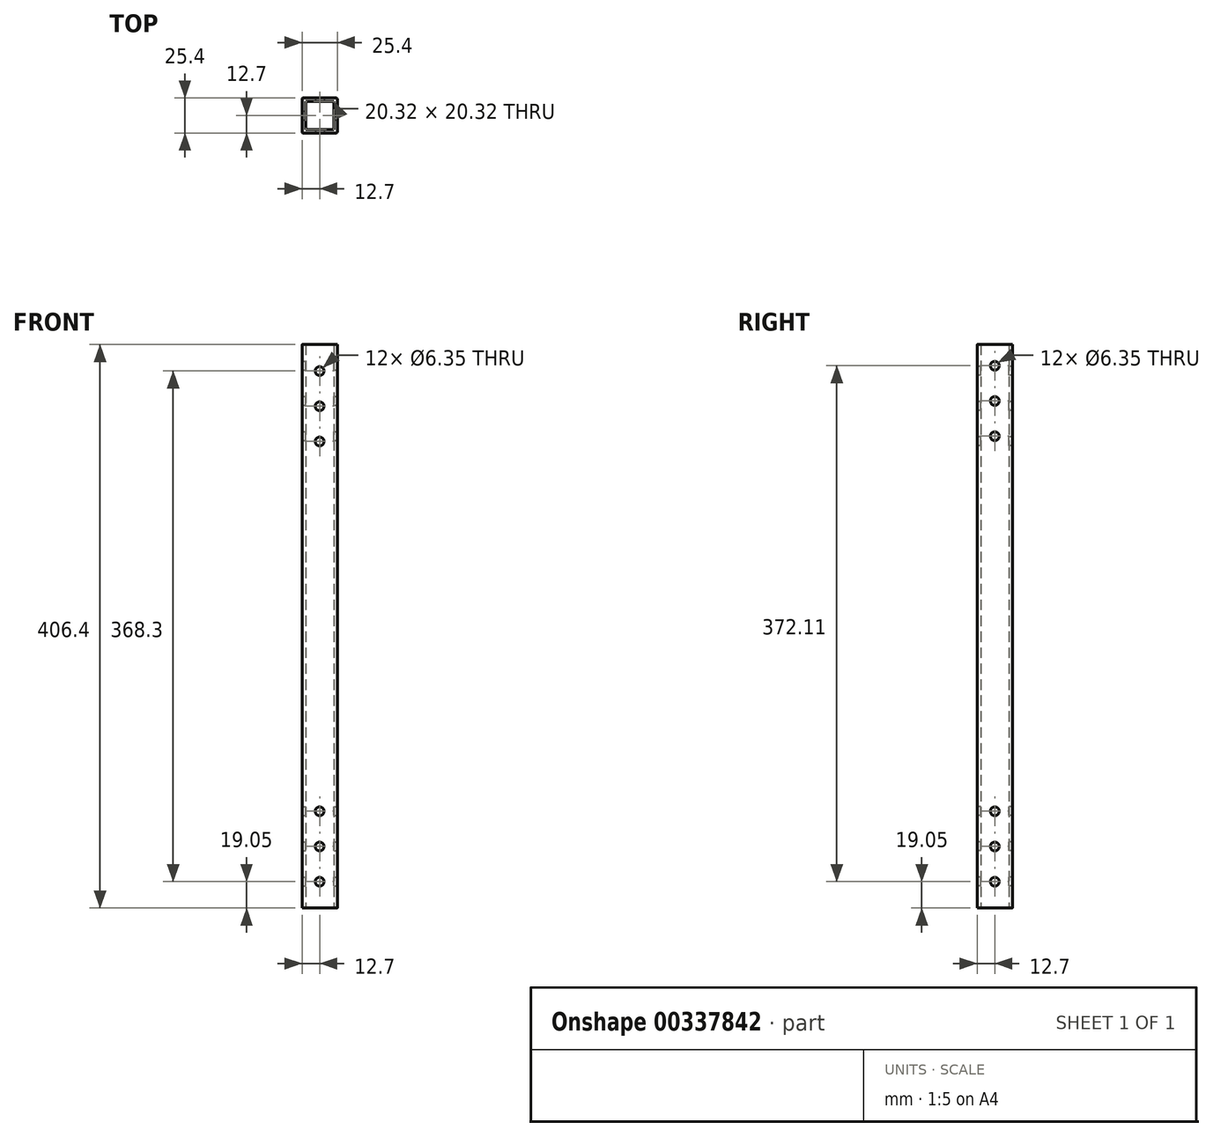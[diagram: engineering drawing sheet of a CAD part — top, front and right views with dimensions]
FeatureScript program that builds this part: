
annotation { "Feature Type Name" : "Feature", "Feature Type Description" : "" }
export const myFeature = defineFeature(function(context is Context, id is Id, definition is map)
    precondition{}
    {
        {
            var Q0;
            Q0=qCreatedBy(makeId("Top.planeOp"),FACE);
            var sketch = newSketch(context, id + "F0", { "sketchPlane" : qUnion([Q0])});
            skPoint(sketch, "E0", {"position": v(0, 0) * mm});
            skPoint(sketch, "E1", {"position": v(12.7, 0) * mm});
            skPoint(sketch, "E2", {"position": v(12.7, 12.7) * mm});
            skLineSegment(sketch, "E3.bottom", {"start": v(12.7, 12.7) * mm, "end": v(-12.7, 12.7) * mm});
            skLineSegment(sketch, "E3.top", {"start": v(12.7, -12.7) * mm, "end": v(-12.7, -12.7) * mm});
            skLineSegment(sketch, "E3.left", {"start": v(12.7, 12.7) * mm, "end": v(12.7, -12.7) * mm});
            skLineSegment(sketch, "E3.right", {"start": v(-12.7, 12.7) * mm, "end": v(-12.7, -12.7) * mm});
            skPoint(sketch, "E4", {"position": v(-12.7, 12.7) * mm});
            skPoint(sketch, "E5", {"position": v(-12.7, -12.7) * mm});
            skPoint(sketch, "E6", {"position": v(12.7, -12.7) * mm});
            skPoint(sketch, "E7", {"position": v(10.16, 0) * mm});
            skPoint(sketch, "E8", {"position": v(10.16, 10.16) * mm});
            skLineSegment(sketch, "E9.bottom", {"start": v(10.16, 10.16) * mm, "end": v(-10.16, 10.16) * mm});
            skLineSegment(sketch, "E9.top", {"start": v(10.16, -10.16) * mm, "end": v(-10.16, -10.16) * mm});
            skLineSegment(sketch, "E9.left", {"start": v(10.16, 10.16) * mm, "end": v(10.16, -10.16) * mm});
            skLineSegment(sketch, "E9.right", {"start": v(-10.16, 10.16) * mm, "end": v(-10.16, -10.16) * mm});
            skSolve(sketch);
        }
        {
            var Q0;
            Q0=makeQuery(id+"F0.imprint","IMPRINT",FACE,{"disambiguationData":[TD([[makeQuery(id+"F0.imprint","IMPRINT",EDGE,{"derivedFrom":sQuery(id+"F0.wireOp",EDGE,"E3.bottom")}),1.0]])]});
            extrude(context, id + "F1", {"entities" : qUnion([Q0]), "depth" : 406.4 * mm});
        }
        {
            var Q0;
            Q0=makeQuery(id+"F1.opExtrude","SWEPT_EDGE",EDGE,{"disambiguationData":[OSD([sQuery(id+"F0.wireOp",EDGE,"E3.bottom"),sQuery(id+"F0.wireOp",EDGE,"E3.left")])]});
            var Q1;
            Q1=makeQuery(id+"F1.opExtrude","SWEPT_EDGE",EDGE,{"disambiguationData":[OSD([sQuery(id+"F0.wireOp",EDGE,"E3.bottom"),sQuery(id+"F0.wireOp",EDGE,"E3.right")])]});
            var Q2;
            Q2=makeQuery(id+"F1.opExtrude","SWEPT_EDGE",EDGE,{"disambiguationData":[OSD([sQuery(id+"F0.wireOp",EDGE,"E3.top"),sQuery(id+"F0.wireOp",EDGE,"E3.right")])]});
            var Q3;
            Q3=makeQuery(id+"F1.opExtrude","SWEPT_EDGE",EDGE,{"disambiguationData":[OSD([sQuery(id+"F0.wireOp",EDGE,"E3.top"),sQuery(id+"F0.wireOp",EDGE,"E3.left")])]});
            fillet(context, id + "F2", {"entities" : qUnion([Q0, Q1, Q2, Q3]), "radius" : 0.76 * mm, "tangentPropagation" : true, "allowEdgeOverflow" : false});
        }
        {
            var Q0;
            Q0=qCreatedBy(makeId("Right.planeOp"),FACE);
            cPlane(context, id + "F3", {"entities" : qUnion([Q0]), "cplaneType" : CPlaneType.OFFSET, "offset" : 12.7 * mm, "width" : 152.4 * mm, "height" : 152.4 * mm});
        }
        {
            var Q0;
            Q0=qCreatedBy(id+"F3.planeOp",FACE);
            var sketch = newSketch(context, id + "F4", { "sketchPlane" : qUnion([Q0])});
            skPoint(sketch, "E10", {"position": v(0, 0) * mm});
            skPoint(sketch, "E11", {"position": v(0, 19.05) * mm});
            skPoint(sketch, "E12", {"position": v(0, 44.45) * mm});
            skPoint(sketch, "E13", {"position": v(0, 391.16) * mm});
            skPoint(sketch, "E14", {"position": v(0, 365.76) * mm});
            skPoint(sketch, "E15", {"position": v(0, 340.36) * mm});
            skPoint(sketch, "E16", {"position": v(0, 69.85) * mm});
            skSolve(sketch);
        }
        {
            var Q0;
            Q0=sQuery(id+"F4.wireOp",VERTEX,"E13");
            var Q1;
            Q1=sQuery(id+"F4.wireOp",VERTEX,"E14");
            var Q2;
            Q2=sQuery(id+"F4.wireOp",VERTEX,"E15");
            var Q3;
            Q3=sQuery(id+"F4.wireOp",VERTEX,"E16");
            var Q4;
            Q4=sQuery(id+"F4.wireOp",VERTEX,"E12");
            var Q5;
            Q5=sQuery(id+"F4.wireOp",VERTEX,"E11");
            var Q6;
            Q6=makeQuery(id+"F1.opExtrude","SWEPT_BODY",BODY,{"disambiguationData":[OSD([sQuery(id+"F0.wireOp",EDGE,"E3.bottom"),sQuery(id+"F0.wireOp",EDGE,"E3.top"),sQuery(id+"F0.wireOp",EDGE,"E3.left"),sQuery(id+"F0.wireOp",EDGE,"E3.right"),sQuery(id+"F0.wireOp",EDGE,"E9.bottom"),sQuery(id+"F0.wireOp",EDGE,"E9.top"),sQuery(id+"F0.wireOp",EDGE,"E9.left"),sQuery(id+"F0.wireOp",EDGE,"E9.right")])]});
            hole(context, id + "F5", {"style" : HoleStyle.SIMPLE, "endStyle" : HoleEndStyle.THROUGH, "holeDiameter" : 6.35 * mm, "tappedDepth" : 12.7 * mm, "tapClearance" : 3, "locations" : qUnion([Q0, Q1, Q2, Q3, Q4, Q5]), "scope" : qUnion([Q6])});
        }
        {
            var Q0;
            Q0=qCreatedBy(makeId("Front.planeOp"),FACE);
            cPlane(context, id + "F6", {"entities" : qUnion([Q0]), "cplaneType" : CPlaneType.OFFSET, "offset" : 12.7 * mm, "width" : 152.4 * mm, "height" : 152.4 * mm});
        }
        {
            var Q0;
            Q0=qCreatedBy(id+"F6.planeOp",FACE);
            var sketch = newSketch(context, id + "F7", { "sketchPlane" : qUnion([Q0])});
            skPoint(sketch, "E17", {"position": v(0, 0) * mm});
            skPoint(sketch, "E18", {"position": v(0, 19.05) * mm});
            skPoint(sketch, "E19", {"position": v(0, 44.45) * mm});
            skPoint(sketch, "E20", {"position": v(0, 387.35) * mm});
            skPoint(sketch, "E21", {"position": v(0, 361.95) * mm});
            skPoint(sketch, "E22", {"position": v(0, 336.55) * mm});
            skPoint(sketch, "E23", {"position": v(0, 69.85) * mm});
            skPoint(sketch, "E24", {"position": v(0, 406.4) * mm});
            skSolve(sketch);
        }
        {
            var Q0;
            Q0=sQuery(id+"F7.wireOp",VERTEX,"E18");
            var Q1;
            Q1=sQuery(id+"F7.wireOp",VERTEX,"E19");
            var Q2;
            Q2=sQuery(id+"F7.wireOp",VERTEX,"E23");
            var Q3;
            Q3=sQuery(id+"F7.wireOp",VERTEX,"E22");
            var Q4;
            Q4=sQuery(id+"F7.wireOp",VERTEX,"E21");
            var Q5;
            Q5=sQuery(id+"F7.wireOp",VERTEX,"E20");
            var Q6;
            Q6=makeQuery(id+"F1.opExtrude","SWEPT_BODY",BODY,{"disambiguationData":[OSD([sQuery(id+"F0.wireOp",EDGE,"E3.bottom"),sQuery(id+"F0.wireOp",EDGE,"E3.top"),sQuery(id+"F0.wireOp",EDGE,"E3.left"),sQuery(id+"F0.wireOp",EDGE,"E3.right"),sQuery(id+"F0.wireOp",EDGE,"E9.bottom"),sQuery(id+"F0.wireOp",EDGE,"E9.top"),sQuery(id+"F0.wireOp",EDGE,"E9.left"),sQuery(id+"F0.wireOp",EDGE,"E9.right")])]});
            hole(context, id + "F8", {"style" : HoleStyle.SIMPLE, "endStyle" : HoleEndStyle.THROUGH, "holeDiameter" : 6.35 * mm, "tappedDepth" : 12.7 * mm, "tapClearance" : 3, "locations" : qUnion([Q0, Q1, Q2, Q3, Q4, Q5]), "scope" : qUnion([Q6])});
        }
        {
            var Q0;
            Q0=qCreatedBy(makeId("Top.planeOp"),FACE);
            cPlane(context, id + "F9", {"entities" : qUnion([Q0]), "cplaneType" : CPlaneType.OFFSET, "offset" : 406.4 * mm, "width" : 152.4 * mm, "height" : 152.4 * mm});
        }
    });
